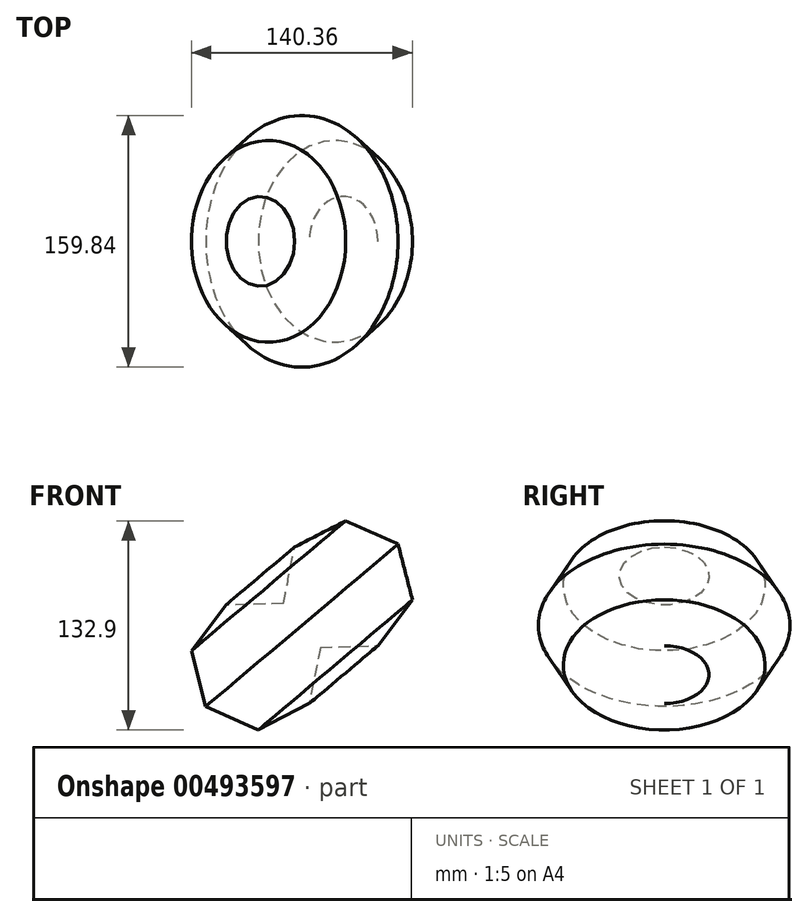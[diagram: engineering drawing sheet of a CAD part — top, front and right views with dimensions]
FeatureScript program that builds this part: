
annotation { "Feature Type Name" : "Feature", "Feature Type Description" : "" }
export const myFeature = defineFeature(function(context is Context, id is Id, definition is map)
    precondition{}
    {
        {
            var Q0;
            Q0=qCreatedBy(makeId("Front.planeOp"),FACE);
            var sketch = newSketch(context, id + "F0", { "sketchPlane" : qUnion([Q0])});
            skCircle(sketch, "E0.cCircle", {"center": v(0, 0) * mm, "radius": 42.04 * mm, "construction": true});
            skLineSegment(sketch, "E0.0", {"start": v(-32.13, -27.11) * mm, "end": v(-41.23, 8.22) * mm});
            skLineSegment(sketch, "E0.1", {"start": v(-41.23, 8.22) * mm, "end": v(-19.28, 37.36) * mm});
            skLineSegment(sketch, "E0.2", {"start": v(-19.28, 37.36) * mm, "end": v(17.19, 38.37) * mm});
            skLineSegment(sketch, "E0.3", {"start": v(17.19, 38.37) * mm, "end": v(40.71, 10.48) * mm});
            skLineSegment(sketch, "E0.4", {"start": v(40.71, 10.48) * mm, "end": v(33.58, -25.3) * mm});
            skLineSegment(sketch, "E0.5", {"start": v(33.58, -25.3) * mm, "end": v(1.16, -42.02) * mm});
            skLineSegment(sketch, "E0.6", {"start": v(1.16, -42.02) * mm, "end": v(-32.13, -27.11) * mm});
            skSolve(sketch);
        }
        {
            var Q0;
            Q0=makeQuery(id+"F0.imprint","IMPRINT",FACE,{"disambiguationData":[TD([[makeQuery(id+"F0.imprint","IMPRINT",EDGE,{"derivedFrom":sQuery(id+"F0.wireOp",EDGE,"E0.0")}),-1.0]])]});
            var Q1;
            Q1=sQuery(id+"F0.wireOp",EDGE,"E0.3");
            revolve(context, id + "F1", {"entities" : qUnion([Q0]), "axis" : qUnion([Q1]), "revolveType" : RevolveType.FULL});
        }
    });
